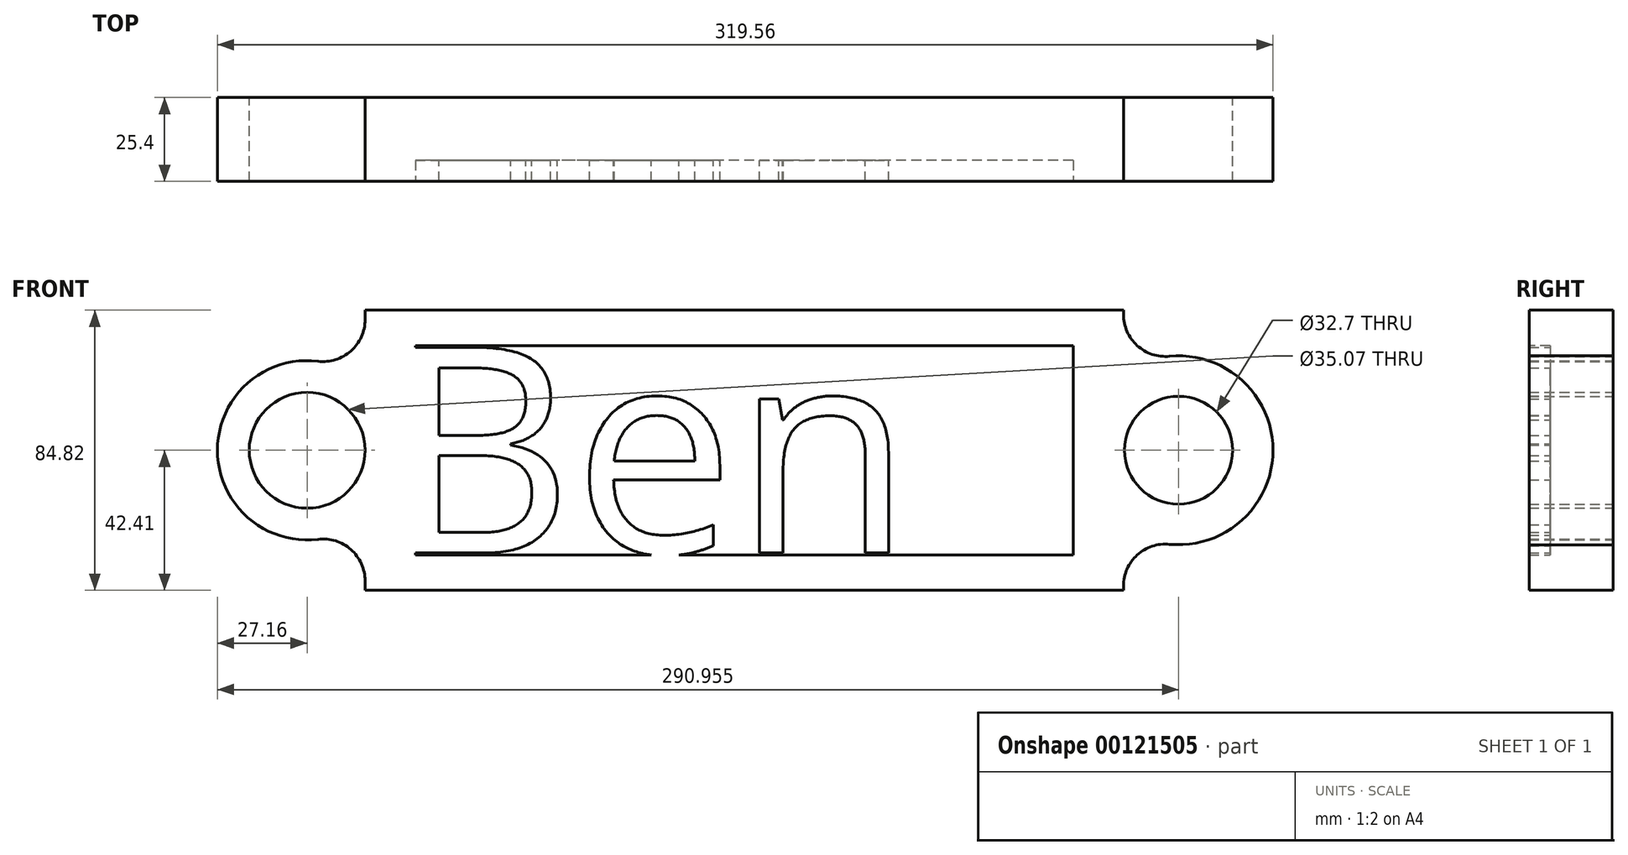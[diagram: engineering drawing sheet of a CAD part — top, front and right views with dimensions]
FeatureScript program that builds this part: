
annotation { "Feature Type Name" : "Feature", "Feature Type Description" : "" }
export const myFeature = defineFeature(function(context is Context, id is Id, definition is map)
    precondition{}
    {
        {
            var Q0;
            Q0=qCreatedBy(makeId("Front.planeOp"),FACE);
            var sketch = newSketch(context, id + "F0", { "sketchPlane" : qUnion([Q0])});
            skLineSegment(sketch, "E0.bottom", {"start": v(114.8, 42.41) * mm, "end": v(-114.8, 42.41) * mm});
            skLineSegment(sketch, "E0.top", {"start": v(114.8, -42.41) * mm, "end": v(-114.8, -42.41) * mm});
            skLineSegment(sketch, "E0.left", {"start": v(114.8, 42.41) * mm, "end": v(114.8, 41.1) * mm});
            skLineSegment(sketch, "E0.right", {"start": v(-114.8, 42.41) * mm, "end": v(-114.8, 39.56) * mm});
            skPoint(sketch, "E0.middle", {"position": v(0, 0) * mm});
            skLineSegment(sketch, "E1.bottom", {"start": v(0, 0) * mm, "end": v(0, 0) * mm});
            skLineSegment(sketch, "E1.top", {"start": v(0, 0) * mm, "end": v(0, 0) * mm});
            skLineSegment(sketch, "E1.left", {"start": v(0, 0) * mm, "end": v(0, 0) * mm});
            skLineSegment(sketch, "E1.right", {"start": v(0, 0) * mm, "end": v(0, 0) * mm});
            skLineSegment(sketch, "E2", {"start": v(114.8, 0) * mm, "end": v(115.11, 0) * mm});
            skPoint(sketch, "E2.endSnap0", {"position": v(114.8, 0) * mm});
            skLineSegment(sketch, "E3", {"start": v(131.46, 0) * mm, "end": v(131.46, 0) * mm});
            skPoint(sketch, "E4.startSnap0", {"position": v(-114.8, 0) * mm});
            skCircle(sketch, "E5", {"center": v(131.46, 0) * mm, "radius": 16.35 * mm});
            skArc(sketch, "E6", {"start": v(128.72, -28.47) * mm, "mid": v(160.07, 0) * mm, "end": v(128.72, 28.47) * mm});
            skCircle(sketch, "E7", {"center": v(-132.33, 0) * mm, "radius": 17.53 * mm});
            skArc(sketch, "E8", {"start": v(-129.04, 26.96) * mm, "mid": v(-159.49, 0) * mm, "end": v(-129.04, -26.96) * mm});
            skLineSegment(sketch, "E9.trimOffspring", {"start": v(-114.8, -39.56) * mm, "end": v(-114.8, -42.41) * mm});
            skPoint(sketch, "E4.end.orphan", {"position": v(-114.8, 0) * mm});
            skLineSegment(sketch, "E10.trimOffspring", {"start": v(114.8, -41.1) * mm, "end": v(114.8, -42.41) * mm});
            skPoint(sketch, "E11.visualSharp", {"position": v(-114.8, 20.74) * mm});
            skArc(sketch, "E11.filletArc", {"start": v(-129.04, 26.96) * mm, "mid": v(-119.08, 30.05) * mm, "end": v(-114.8, 39.56) * mm});
            skPoint(sketch, "E12.visualSharp", {"position": v(-114.8, -20.74) * mm});
            skArc(sketch, "E12.filletArc", {"start": v(-114.8, -39.56) * mm, "mid": v(-119.08, -30.05) * mm, "end": v(-129.04, -26.96) * mm});
            skPoint(sketch, "E13.visualSharp", {"position": v(114.8, 23.24) * mm});
            skArc(sketch, "E13.filletArc", {"start": v(114.8, 41.1) * mm, "mid": v(118.96, 31.7) * mm, "end": v(128.72, 28.47) * mm});
            skPoint(sketch, "E14.visualSharp", {"position": v(114.8, -23.24) * mm});
            skArc(sketch, "E14.filletArc", {"start": v(128.72, -28.47) * mm, "mid": v(118.96, -31.7) * mm, "end": v(114.8, -41.1) * mm});
            skLineSegment(sketch, "E15.bottom", {"start": v(104.01, 30.44) * mm, "end": v(-104.01, 30.44) * mm});
            skLineSegment(sketch, "E15.top", {"start": v(104.01, -30.44) * mm, "end": v(-104.01, -30.44) * mm});
            skLineSegment(sketch, "E15.left", {"start": v(104.01, 30.44) * mm, "end": v(104.01, -30.44) * mm});
            skLineSegment(sketch, "E15.right", {"start": v(-104.01, 30.44) * mm, "end": v(-104.01, -30.44) * mm});
            skSolve(sketch);
        }
        {
            var Q0;
            Q0=makeQuery(id+"F0.imprint","IMPRINT",FACE,{"disambiguationData":[TD([[makeQuery(id+"F0.imprint","IMPRINT",EDGE,{"derivedFrom":sQuery(id+"F0.wireOp",EDGE,"E0.bottom")}),1.0]])]});
            var Q1;
            Q1=makeQuery(id+"F0.imprint","IMPRINT",FACE,{"disambiguationData":[TD([[makeQuery(id+"F0.imprint","IMPRINT",EDGE,{"derivedFrom":sQuery(id+"F0.wireOp",EDGE,"E15.bottom")}),1.0]])]});
            extrude(context, id + "F1", {"entities" : qUnion([Q0, Q1]), "depth" : 25.4 * mm});
        }
        {
            var Q0;
            Q0=makeQuery(id+"F1.opExtrude","CAP_FACE",FACE,{"disambiguationData":[OSD([sQuery(id+"F0.wireOp",EDGE,"E0.bottom"),sQuery(id+"F0.wireOp",EDGE,"E0.top"),sQuery(id+"F0.wireOp",EDGE,"E0.left"),sQuery(id+"F0.wireOp",EDGE,"E0.right"),sQuery(id+"F0.wireOp",EDGE,"E5"),sQuery(id+"F0.wireOp",EDGE,"E6"),sQuery(id+"F0.wireOp",EDGE,"E7"),sQuery(id+"F0.wireOp",EDGE,"E8"),sQuery(id+"F0.wireOp",EDGE,"E9.trimOffspring"),sQuery(id+"F0.wireOp",EDGE,"E10.trimOffspring"),sQuery(id+"F0.wireOp",EDGE,"E11.filletArc"),sQuery(id+"F0.wireOp",EDGE,"E12.filletArc"),sQuery(id+"F0.wireOp",EDGE,"E13.filletArc"),sQuery(id+"F0.wireOp",EDGE,"E14.filletArc")])],"isStart":false});
            var sketch = newSketch(context, id + "F2", { "sketchPlane" : qUnion([Q0])});
            skLineSegment(sketch, "E16.bottom", {"start": v(99.57, 31.7) * mm, "end": v(-99.57, 31.7) * mm});
            skLineSegment(sketch, "E16.top", {"start": v(99.57, -31.7) * mm, "end": v(-99.57, -31.7) * mm});
            skLineSegment(sketch, "E16.left", {"start": v(99.57, 31.7) * mm, "end": v(99.57, -31.7) * mm});
            skLineSegment(sketch, "E16.right", {"start": v(-99.57, 31.7) * mm, "end": v(-99.57, -31.7) * mm});
            skPoint(sketch, "E16.middle", {"position": v(0, 0) * mm});
            skPoint(sketch, "E16.cornerSnap0", {"position": v(118.96, 31.7) * mm});
            skSolve(sketch);
        }
        {
            var Q0;
            Q0=makeQuery(id+"F2.imprint","IMPRINT",FACE,{"disambiguationData":[TD([[makeQuery(id+"F2.imprint","IMPRINT",EDGE,{"derivedFrom":sQuery(id+"F2.wireOp",EDGE,"E16.bottom")}),1.0]])]});
            extrude(context, id + "F3", {"entities" : qUnion([Q0]), "operationType" : NewBodyOperationType.REMOVE, "oppositeDirection" : true, "depth" : 6.35 * mm});
        }
        {
            var Q0;
            Q0=makeQuery(id+"F3.boolean.opBoolean","COPY",FACE,{"derivedFrom":makeQuery(id+"F3.opExtrude","CAP_FACE",FACE,{"disambiguationData":[OSD([sQuery(id+"F2.wireOp",EDGE,"E16.bottom"),sQuery(id+"F2.wireOp",EDGE,"E16.top"),sQuery(id+"F2.wireOp",EDGE,"E16.left"),sQuery(id+"F2.wireOp",EDGE,"E16.right")])],"isStart":false})});
            var sketch = newSketch(context, id + "F4", { "sketchPlane" : qUnion([Q0])});
            skText(sketch, "E17", { "text": "BenF", "fontName": "OpenSans-Regular.ttf"});
            const initialGuessF4  = {"E17": [-0.10824, -0.03106, 1, 0, 0.06277]};
            skSetInitialGuess(sketch, initialGuessF4);
            skSolve(sketch);
        }
        {
            var Q0;
            Q0=makeQuery(id+"F4.imprint","IMPRINT",FACE,{"disambiguationData":[TD([[makeQuery(id+"F4.imprint","IMPRINT",EDGE,{"derivedFrom":sQuery(id+"F4.wireOp",EDGE,"E17.sketch_text.stroke-44")}),-1.0]])]});
            var Q1;
            {var subQ0=sQuery(id+"F4.wireOp",EDGE,"E17.sketch_text.stroke-1");Q1=makeQuery(id+"F4.imprint","IMPRINT",FACE,{"disambiguationData":[TD([[makeQuery(id+"F4.imprint","IMPRINT",EDGE,{"derivedFrom":subQ0}),-1.0]])]});}
            var Q2;
            {var subQ0=sQuery(id+"F4.wireOp",EDGE,"E17.sketch_text.stroke-26");Q2=makeQuery(id+"F4.imprint","IMPRINT",FACE,{"disambiguationData":[TD([[makeQuery(id+"F4.imprint","IMPRINT",EDGE,{"derivedFrom":subQ0}),-1.0]])]});}
            extrude(context, id + "F6", {"entities" : qUnion([Q0, Q1, Q2]), "operationType" : NewBodyOperationType.ADD, "depth" : 6.35 * mm});
        }
    });
